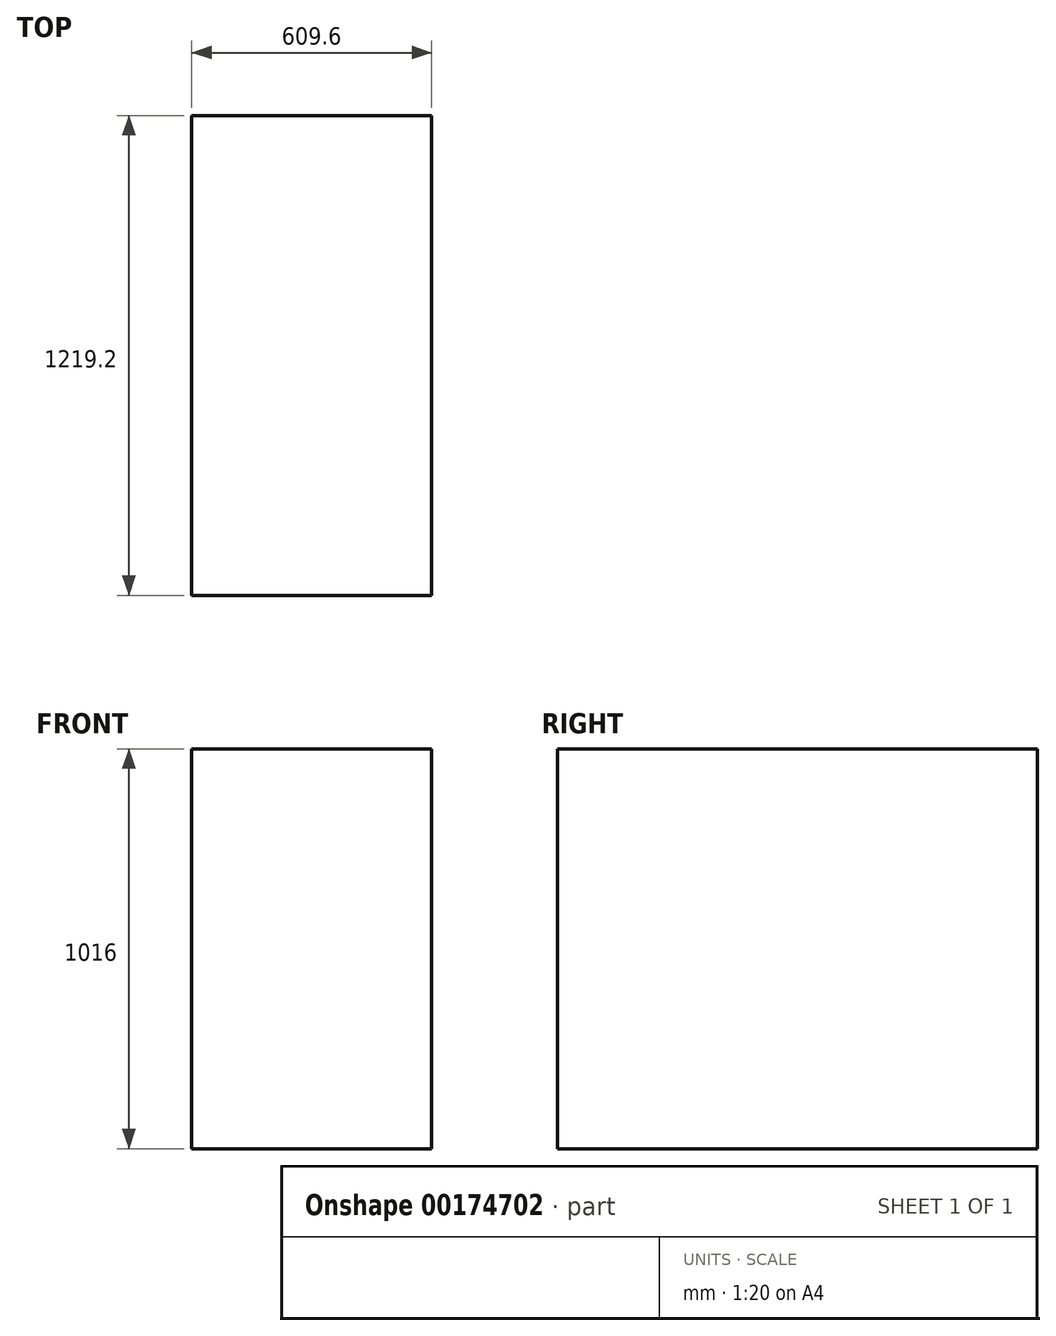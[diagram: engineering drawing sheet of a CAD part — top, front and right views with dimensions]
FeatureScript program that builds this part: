
annotation { "Feature Type Name" : "Feature", "Feature Type Description" : "" }
export const myFeature = defineFeature(function(context is Context, id is Id, definition is map)
    precondition{}
    {
        {
            var Q0;
            Q0=qCreatedBy(makeId("Top.planeOp"),FACE);
            var sketch = newSketch(context, id + "F0", { "sketchPlane" : qUnion([Q0])});
            skLineSegment(sketch, "E0.bottom", {"start": v(304.8, -609.6) * mm, "end": v(-304.8, -609.6) * mm});
            skLineSegment(sketch, "E0.top", {"start": v(304.8, 609.6) * mm, "end": v(-304.8, 609.6) * mm});
            skLineSegment(sketch, "E0.left", {"start": v(304.8, -609.6) * mm, "end": v(304.8, 609.6) * mm});
            skLineSegment(sketch, "E0.right", {"start": v(-304.8, -609.6) * mm, "end": v(-304.8, 609.6) * mm});
            skPoint(sketch, "E0.middle", {"position": v(0, 0) * mm});
            skSolve(sketch);
        }
        {
            var Q0;
            Q0 = qSketchRegion(id + "F0", true);
            extrude(context, id + "F1", {"entities" : qUnion([Q0]), "depth" : 1016 * mm});
        }
    });
